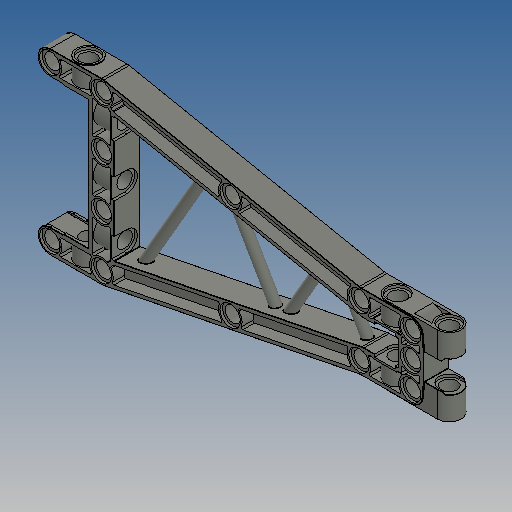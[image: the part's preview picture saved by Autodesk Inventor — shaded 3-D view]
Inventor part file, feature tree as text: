
AUTODESK INVENTOR PART (.ipt)
format: ipt  version: 2025 (Build 290162010, 162A)  size: 1,337,856 bytes
history: native  units: mm
features: sketch x21, extrude x17, revolve x4, hole x3, fillet x3, projected_geometry x3, delete_face x2, mirror x2, direct_edit x1, move_body x1
ambient origin geometry x8: Origin, YZ Plane, XZ Plane, XY Plane, X Axis, Y Axis, Z Axis, Center Point
bodies: Volumenkörper1 (feature_tree)
feature tree (57):
  extrude  "Extrusion1"  Depth=8.0mm
  extrude  "Extrusion2"  Depth=16.0mm
  extrude  "Extrusion3"  Depth=4.0mm
  extrude  "Extrusion4"  Depth=96.0mm
  extrude  "Extrusion5"  Depth=16.0mm
  extrude  "Extrusion10"  Depth=40.792156mm
  delete_face  "Fläche löschen1"
  extrude  "Extrusion6"  Depth=3.7mm
  extrude  "Extrusion7"  Depth=3.7mm
  extrude  "Extrusion8"  Depth=3.7mm
  extrude  "Extrusion9"  Depth=4.0mm TaperAngle=0.0deg
  hole  "Bohrung1"  [1 undecoded]
  hole  "Bohrung2"  [1 undecoded]
  hole  "Bohrung3"  [1 undecoded]
  extrude  "Extrusion11"  Depth=1.1mm
  extrude  "Extrusion12"  Depth=2.8mm
  extrude  "Extrusion13"  Depth=2.8mm
  extrude  "Extrusion14"  Depth=0.4mm
  fillet  "Rundung1"  Radius=0.5mm
  mirror  "Spiegeln1"
  extrude  "Extrusion15"  Depth=0.5mm
  extrude  "Extrusion16"  Depth=3.6mm TaperAngle=0.0deg
  direct_edit  "Direktbearbeitung1"
  extrude  "Extrusion17"  Depth=7.4mm
  fillet  "Rundung2"  Radius=0.3mm
  mirror  "Spiegeln2"
  sketch  "Skizze20"  dims[d45=16.0mm d46=7.4mm d47=0.3mm d48=0.0mm d49=7.7mm d50=0.0mm]
  revolve  "Umdrehung1"
  revolve  "Umdrehung2"
  revolve  "Umdrehung3"
  revolve  "Umdrehung4"
  delete_face  "Fläche löschen2"
  fillet  "Rundung3"  Radius=7.7mm
  sketch  "Skizze1"  dims[d0=4.8mm d1=8.0mm]
  sketch  "Skizze2"  dims[d2=16.0mm d3=16.0mm]
  sketch  "Skizze3"  dims[d4=3.7mm d5=4.0mm]
  sketch  "Skizze4"  dims[d6=4.0mm d7=96.0mm]
  sketch  "Skizze5"  dims[d8=16.0mm d9=16.0mm]
  sketch  "Skizze6"  dims[d10=40.0mm d11=40.792156mm]
  sketch  "Skizze7"  dims[d12=40.792156mm d13=3.7mm]
  sketch  "Skizze8"  dims[d14=4.0mm d15=3.7mm]
  sketch  "Skizze9"  dims[d16=3.7mm d18=3.7mm]
  sketch  "Skizze10"  dims[d20=0.1mm d21=4.0mm d22=0.0mm]
  sketch  "Skizze11"  dims[d23=6.4mm d24=0.8mm d25=0.0mm]
  projected_geometry  "Projizierte Kontur1"
  sketch  "Skizze12"  dims[d26=1.1mm d27=1.1mm]
  sketch  "Skizze13"  dims[d28=1.1mm d30=1.1mm]
  projected_geometry  "Projizierte Kontur2"
  sketch  "Skizze14"  dims[d31=1.1mm d32=1.1mm]
  projected_geometry  "Projizierte Kontur3"
  sketch  "Skizze15"  dims[d33=5.6mm d34=2.8mm]
  sketch  "Skizze16"  dims[d35=5.6mm d36=2.8mm]
  sketch  "Skizze17"  dims[d37=3.7mm d38=0.4mm d39=0.5mm]
  sketch  "Skizze18"  dims[d40=0.5mm d41=0.5mm]
  sketch  "Skizze19"  dims[d42=0.4mm d43=3.6mm d44=0.0mm]
  sketch  "Skizze21"  dims[d51=7.6mm d52=0.0mm d53=7.4mm d54=0.3mm d55=0.0mm d56=16.0mm d57=7.4mm d58=10.0mm d59=0.0mm d60=7.2mm d61=0.0mm d62=4.0mm d63=45.0deg d64=0.4mm d65=0.0mm d66=4.8mm d67=6.0mm d68=6.4mm d69=0.8mm d70=90.0deg d71=8.0mm d72=20.594885mm d73=4.8mm d74=6.0mm d75=6.4mm d76=0.8mm d77=90.0deg d78=8.0mm d79=20.594885mm d80=2.8mm d82=10.0mm d83=0.0mm d84=10.0mm d85=0.0mm d86=3.6mm d87=4.8mm d88=6.0mm d89=6.4mm d90=0.8mm d91=90.0deg d92=8.0mm d93=20.594885mm d94=6.4mm d95=0.8mm d96=0.0mm d97=0.8mm d98=0.0mm d99=45.0deg d100=0.0mm d101=0.0mm d102=0.1mm d103=6.0mm d104=0.8mm d105=0.0mm d106=0.5mm d107=0.0mm d108=0.0mm d109=0.0mm d110=0.3mm d111=45.0deg d112=0.4mm d113=0.0mm d114=0.4mm d116=30.0deg d117=30.0deg d121=4.5mm d122=34.5mm d123=27.5mm d124=44.5mm d125=1.5mm d126=90.0deg d127=90.0deg d128=90.0deg d129=90.0deg d130=0.1mm]
  move_body  "Verschieben1"
note: 3 required parameter values undecoded (feature->parameter linkage not recoverable at this tier; creation-order binding heuristic only, values carry confidence <= 0.55)
